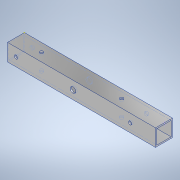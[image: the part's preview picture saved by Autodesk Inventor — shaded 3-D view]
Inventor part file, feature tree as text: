
AUTODESK INVENTOR PART (.ipt)
format: ipt  version: 2020.3 (Build 243373000, 373)  size: 177,664 bytes
history: native  units: mm
features: sketch x8, hole x6, extrude x2, other x1
ambient origin geometry x8: Origin, YZ Plane, XZ Plane, XY Plane, X Axis, Y Axis, Z Axis, Center Point
bodies: Body1 (feature_tree)
feature tree (17):
  other  "ソリッド1"
  extrude  "押し出し1"  Depth=15.0mm
  hole  "穴1"  [1 undecoded]
  hole  "穴2"  [1 undecoded]
  hole  "穴3"  [1 undecoded]
  extrude  "押し出し2"  Depth=1.2mm
  hole  "穴4"  [1 undecoded]
  hole  "穴5"  [1 undecoded]
  hole  "穴6"  [1 undecoded]
  sketch  "スケッチ1"
  sketch  "スケッチ2"
  sketch  "スケッチ3"
  sketch  "スケッチ4"
  sketch  "スケッチ5"
  sketch  "スケッチ6"
  sketch  "スケッチ7"
  sketch  "スケッチ8"
note: 6 required parameter values undecoded (feature->parameter linkage not recoverable at this tier; creation-order binding heuristic only, values carry confidence <= 0.55)
